# Revit family: Haworth_Cappellini_Bac_Table_Rectangle_AP_PRELIMINARY
name_source: partatom
category: Furniture
revit_build: Autodesk Revit 2018 (Build: 20170223_1515(x64)
units: mm (PartAtom-declared; Revit-internal decimal feet)

## family parameters
Always vertical = Yes
Cut with Voids When Loaded = No
OmniClass Number = 23.40.70.14.64.21
OmniClass Title = Systems Furniture
Room Calculation Point = No
Shared = No
Work Plane-Based = No

## types (2) — shared parameters
Actual Depth = 850 mm  [stored 2.78871 ft]
Actual Height = 740 mm  [stored 2.42782 ft]
Assembly Code = E2020200
Description = Haworth - Cappellini - Bac - Table - Rectangle
Leg Depth = 100 mm  [stored 0.328084 ft]
Manufacturer = Haworth
Model = BACX
Revision Number = 4
Size = Verify Final Dim. w/ Haworth
Support Depth = 60 mm
Support Height = 110 mm  [stored 0.360892 ft]
Support Offset = 200 mm  [stored 0.656168 ft]
Table Thickness = 25 mm  [stored 0.082021 ft]
URL = https://www.haworth.com
URL - Product = https://www.haworth.com
Warranty = http://www.haworth.com

## per-type parameters (varying)
| type | Actual Width | Large | Small |
| Small Table | 2000 mm  [stored 6.56168 ft] | No | Yes |
| Large Table | 2400 mm | Yes | No |

note: [stored X ft] marks values corroborated as IEEE doubles in the binary element streams (Revit-internal decimal feet)

## geometry (parser evidence)
native form markers: Sweep x2
no freeform markers — native parametric forms only
